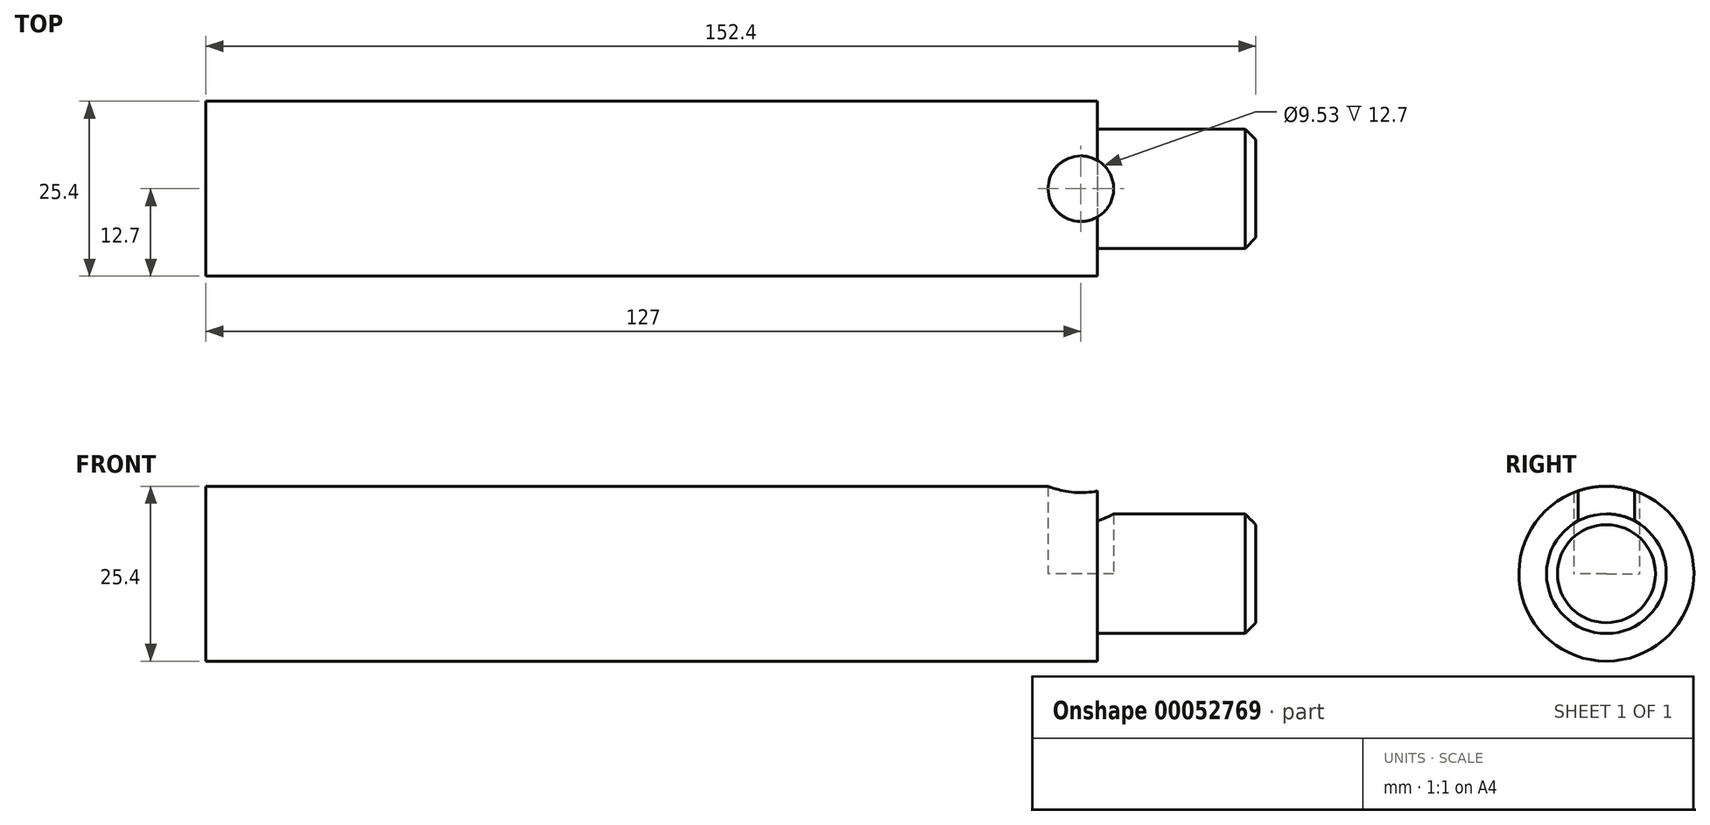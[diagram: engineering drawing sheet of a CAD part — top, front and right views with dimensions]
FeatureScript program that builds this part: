
annotation { "Feature Type Name" : "Feature", "Feature Type Description" : "" }
export const myFeature = defineFeature(function(context is Context, id is Id, definition is map)
    precondition{}
    {
        {
            var Q0;
            Q0=qCreatedBy(makeId("Front.planeOp"),FACE);
            var sketch = newSketch(context, id + "F0", { "sketchPlane" : qUnion([Q0])});
            skLineSegment(sketch, "E0", {"start": v(0, 0) * mm, "end": v(0, 7.11) * mm});
            skLineSegment(sketch, "E1", {"start": v(0, 7.11) * mm, "end": v(-1.57, 8.69) * mm});
            skLineSegment(sketch, "E2", {"start": v(-1.57, 8.69) * mm, "end": v(-22.99, 8.69) * mm});
            skLineSegment(sketch, "E3", {"start": v(-22.99, 8.69) * mm, "end": v(-22.99, 12.7) * mm});
            skLineSegment(sketch, "E4", {"start": v(-22.99, 12.7) * mm, "end": v(-152.4, 12.7) * mm});
            skLineSegment(sketch, "E5", {"start": v(-152.4, 12.7) * mm, "end": v(-152.4, 0) * mm});
            skLineSegment(sketch, "E6", {"start": v(-152.4, 0) * mm, "end": v(0, 0) * mm});
            skSolve(sketch);
        }
        {
            var Q0;
            Q0 = qSketchRegion(id + "F0", true);
            var Q1;
            Q1=sQuery(id+"F0.wireOp",EDGE,"E6");
            revolve(context, id + "F1", {"entities" : qUnion([Q0]), "axis" : qUnion([Q1]), "revolveType" : RevolveType.FULL});
        }
        {
            var Q0;
            Q0=qCreatedBy(makeId("Top.planeOp"),FACE);
            var sketch = newSketch(context, id + "F2", { "sketchPlane" : qUnion([Q0])});
            skCircle(sketch, "E7", {"center": v(-25.4, 0) * mm, "radius": 4.76 * mm});
            skSolve(sketch);
        }
        {
            var Q0;
            Q0 = qSketchRegion(id + "F2", true);
            extrude(context, id + "F3", {"entities" : qUnion([Q0]), "operationType" : NewBodyOperationType.REMOVE, "depth" : 25.4 * mm});
        }
    });
